# Revit family: FU_Table_Sandler_Mesa 0114-Base
name_source: partatom
category: Furniture
units: mm (PartAtom-declared; Revit-internal decimal feet)

## family parameters
Always vertical = Yes
Cut with Voids When Loaded = No
OmniClass Number = 23.40.20.00
OmniClass Title = General Furniture and Specialties
Render Appearance Source = Family Geometry
Room Calculation Point = No
Shared = No
Work Plane-Based = No

## types (1)
- Mesa 0014 Base
    Default Elevation = 0 mm  [stored 0 ft]
    Depth = 465 mm  [stored 1.52559 ft]
    Description = Steel table base at bar height. Steel central column, round base plate. Works with Mesa tabletops.
    Height = 1030 mm  [stored 3.37927 ft]
    Manufacturer = Sandler
    Model = Mesa 0014
    URL = https://www.sandlerseating.com
    Width = 465 mm  [stored 1.52559 ft]

note: [stored X ft] marks values corroborated as IEEE doubles in the binary element streams (Revit-internal decimal feet)

## geometry (parser evidence)
native form markers: Sweep x6
no freeform markers — native parametric forms only
